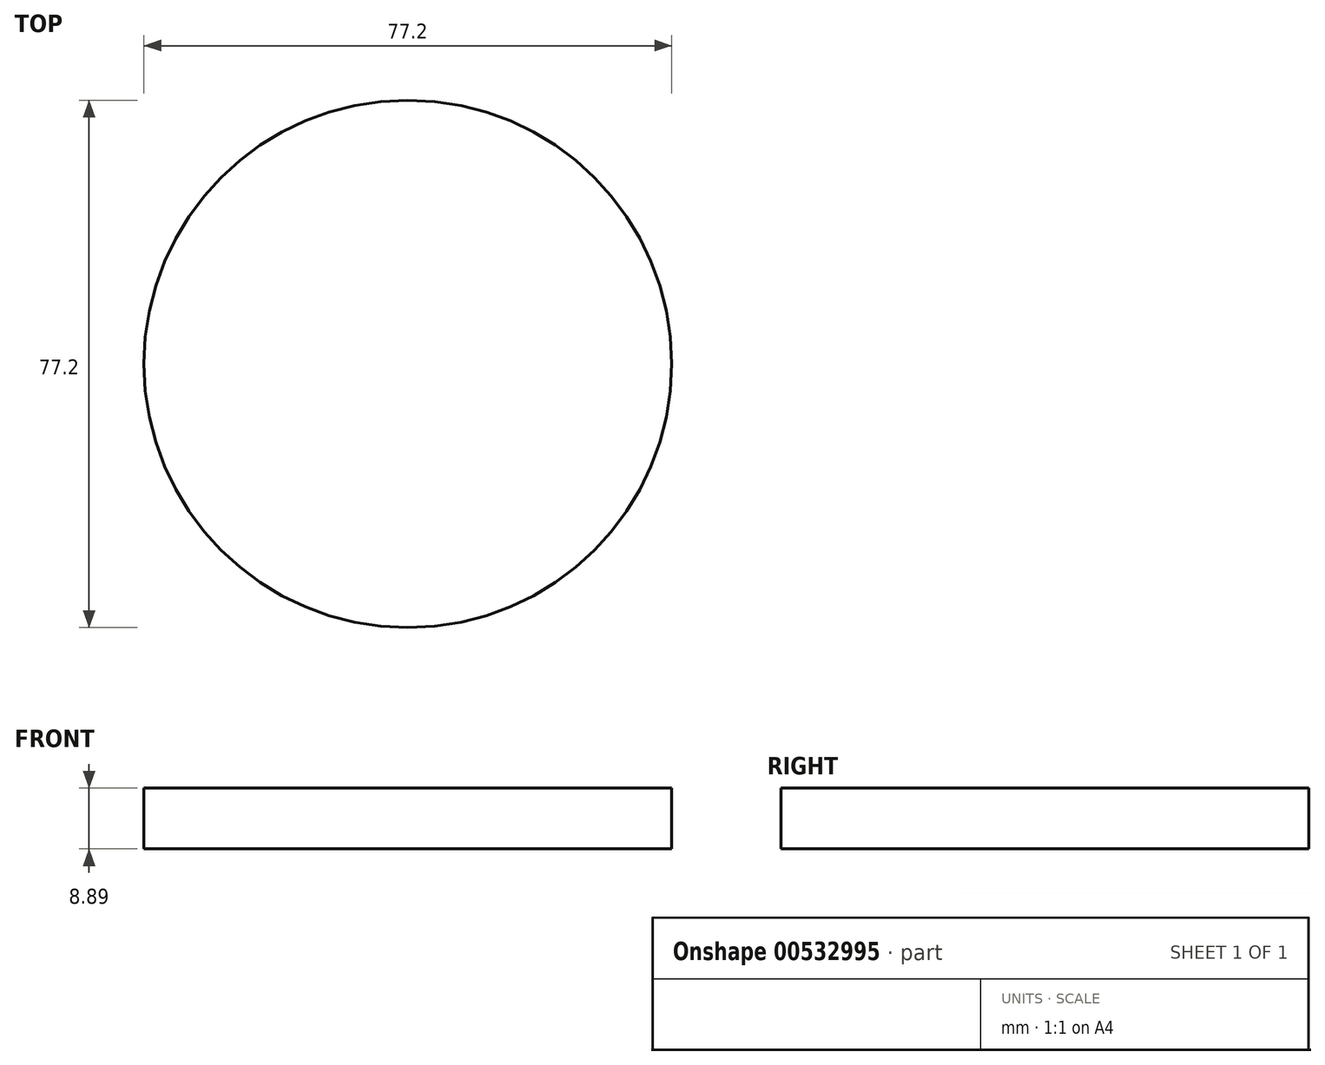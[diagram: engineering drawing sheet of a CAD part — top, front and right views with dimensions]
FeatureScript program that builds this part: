
annotation { "Feature Type Name" : "Feature", "Feature Type Description" : "" }
export const myFeature = defineFeature(function(context is Context, id is Id, definition is map)
    precondition{}
    {
        {
            var Q0;
            Q0=qCreatedBy(makeId("Top.planeOp"),FACE);
            var sketch = newSketch(context, id + "F0", { "sketchPlane" : qUnion([Q0])});
            skCircle(sketch, "E0", {"center": v(0, 0) * mm, "radius": 38.6 * mm});
            skSolve(sketch);
        }
        {
            var Q0;
            Q0=makeQuery(id+"F0.imprint","IMPRINT",FACE,{"disambiguationData":[TD([[makeQuery(id+"F0.imprint","IMPRINT",EDGE,{"derivedFrom":sQuery(id+"F0.wireOp",EDGE,"E0")}),1.0]])]});
            extrude(context, id + "F1", {"entities" : qUnion([Q0]), "depth" : 8.9 * mm, "offsetDistance" : 25.4 * mm});
        }
    });
